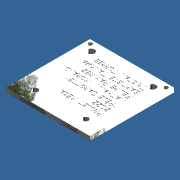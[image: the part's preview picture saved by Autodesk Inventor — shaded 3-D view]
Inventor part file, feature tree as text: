
AUTODESK INVENTOR PART (.ipt)
format: ipt  version: 2018 (Build 220112000, 112)  size: 1,935,872 bytes
history: native  units: mm
features: extrude x4, sketch x4, projected_geometry x1
ambient origin geometry x8: Origin, YZ Plane, XZ Plane, XY Plane, X Axis, Y Axis, Z Axis, Center Point
bodies: Solid1 (feature_tree)
feature tree (9):
  extrude  "Extrusion1"  Depth=100.0mm
  extrude  "Extrusion11"  Depth=25.0mm
  extrude  "Extrusion13"  Depth=3.3mm
  extrude  "Extrusion14"  Depth=5.0mm
  sketch  "Sketch1"  dims[d0=100.0mm d1=100.0mm]
  sketch  "Sketch7"  dims[d2=5.0mm d3=0.0mm d72=25.0mm]
  sketch  "Sketch11"  dims[d77=8.0mm d78=3.3mm]
  projected_geometry  "Projected Loop6"
  sketch  "Sketch13"  dims[d86=5.0mm d88=5.0mm d101=6.6mm d102=6.0mm d103=6.6mm d104=0.0mm d105=0.0mm d111=5.0mm d112=8.5mm d113=10.0mm d114=0.0mm d121=7.0mm d122=5.0mm d123=10.0mm d124=80.0mm d125=60.0mm d126=100.0mm d127=25.0mm d128=1.0mm d129=0.0mm]
